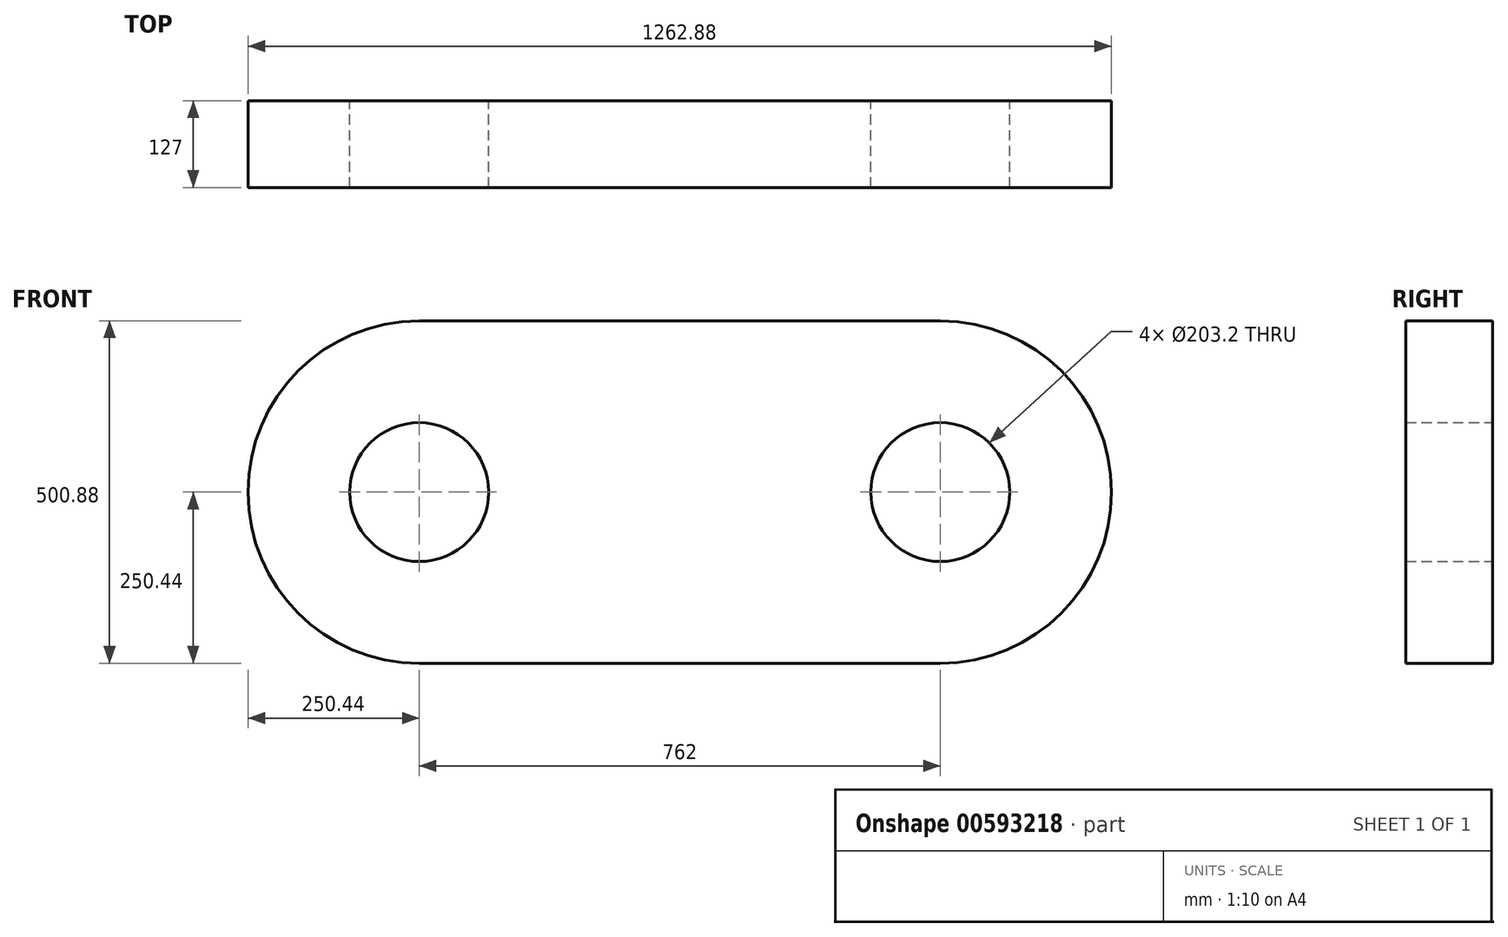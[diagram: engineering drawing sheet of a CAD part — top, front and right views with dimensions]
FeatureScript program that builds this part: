
annotation { "Feature Type Name" : "Feature", "Feature Type Description" : "" }
export const myFeature = defineFeature(function(context is Context, id is Id, definition is map)
    precondition{}
    {
        {
            var Q0;
            Q0=qCreatedBy(makeId("Front.planeOp"),FACE);
            var sketch = newSketch(context, id + "F0", { "sketchPlane" : qUnion([Q0])});
            skLineSegment(sketch, "E0.bottom", {"start": v(-381, 250.44) * mm, "end": v(381, 250.44) * mm});
            skLineSegment(sketch, "E0.top", {"start": v(-381, -250.44) * mm, "end": v(381, -250.44) * mm});
            skLineSegment(sketch, "E0.left", {"start": v(-381, 250.44) * mm, "end": v(-381, -250.44) * mm});
            skLineSegment(sketch, "E0.right", {"start": v(381, 250.44) * mm, "end": v(381, -250.44) * mm});
            skCircle(sketch, "E1", {"center": v(381, 0) * mm, "radius": 250.44 * mm});
            skCircle(sketch, "E2", {"center": v(-381, 0) * mm, "radius": 250.44 * mm});
            skCircle(sketch, "E3", {"center": v(-381, 0) * mm, "radius": 101.6 * mm});
            skCircle(sketch, "E4", {"center": v(381, 0) * mm, "radius": 101.6 * mm});
            skSolve(sketch);
        }
        {
            var Q0;
            {var subQ1=sQuery(id+"F0.wireOp",EDGE,"E0.left");var subQ3=sQuery(id+"F0.wireOp",EDGE,"E3");var subQ4=makeQuery(id+"F0.imprint","INTERSECT",VERTEX,{"disambiguationData":[OD(0.0)],"derivedFrom":[subQ1,subQ3]});Q0=makeQuery(id+"F0.imprint","IMPRINT",FACE,{"disambiguationData":[TD([[makeQuery(id+"F0.imprint","IMPRINT",EDGE,{"disambiguationData":[TD([[subQ4,-1.0]])],"derivedFrom":subQ3}),-1.0]])]});}
            var Q1;
            {var subQ1=sQuery(id+"F0.wireOp",EDGE,"E0.left");var subQ3=sQuery(id+"F0.wireOp",EDGE,"E3");var subQ4=makeQuery(id+"F0.imprint","INTERSECT",VERTEX,{"disambiguationData":[OD(0.0)],"derivedFrom":[subQ1,subQ3]});Q1=makeQuery(id+"F0.imprint","IMPRINT",FACE,{"disambiguationData":[TD([[makeQuery(id+"F0.imprint","IMPRINT",EDGE,{"disambiguationData":[TD([[subQ4,1.0]])],"derivedFrom":subQ3}),-1.0]])]});}
            var Q2;
            {var subQ0=sQuery(id+"F0.wireOp",EDGE,"E0.bottom");Q2=makeQuery(id+"F0.imprint","IMPRINT",FACE,{"disambiguationData":[TD([[makeQuery(id+"F0.imprint","IMPRINT",EDGE,{"derivedFrom":subQ0}),-1.0]])]});}
            var Q3;
            {var subQ1=sQuery(id+"F0.wireOp",EDGE,"E0.right");var subQ3=sQuery(id+"F0.wireOp",EDGE,"E4");var subQ4=makeQuery(id+"F0.imprint","INTERSECT",VERTEX,{"disambiguationData":[OD(0.0)],"derivedFrom":[subQ1,subQ3]});Q3=makeQuery(id+"F0.imprint","IMPRINT",FACE,{"disambiguationData":[TD([[makeQuery(id+"F0.imprint","IMPRINT",EDGE,{"disambiguationData":[TD([[subQ4,-1.0]])],"derivedFrom":subQ3}),-1.0]])]});}
            var Q4;
            {var subQ1=sQuery(id+"F0.wireOp",EDGE,"E0.right");var subQ3=sQuery(id+"F0.wireOp",EDGE,"E4");var subQ4=makeQuery(id+"F0.imprint","INTERSECT",VERTEX,{"disambiguationData":[OD(0.0)],"derivedFrom":[subQ1,subQ3]});Q4=makeQuery(id+"F0.imprint","IMPRINT",FACE,{"disambiguationData":[TD([[makeQuery(id+"F0.imprint","IMPRINT",EDGE,{"disambiguationData":[TD([[subQ4,1.0]])],"derivedFrom":subQ3}),-1.0]])]});}
            extrude(context, id + "F1", {"entities" : qUnion([Q0, Q1, Q2, Q3, Q4]), "depth" : 127 * mm, "offsetDistance" : 25.4 * mm});
        }
    });
